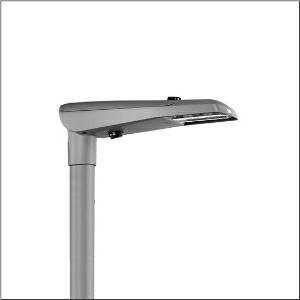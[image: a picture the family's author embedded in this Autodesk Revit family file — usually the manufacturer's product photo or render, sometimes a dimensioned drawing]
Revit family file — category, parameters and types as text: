
# Revit family: streetlight_sl_11_iq_micro___st1_2a_5xc1ac1y08de_0507
name_source: partatom
category: Lighting Fixtures
units: mm (PartAtom-declared; Revit-internal decimal feet)

## family parameters
Cut with Voids When Loaded = No
Host = Face
Light Source = No
Part Type = Normal
Room Calculation Point = No
Round Connector Dimension = Use Diameter
Shared = No

## types (1)
- --- (1 x LED, 3860 lm, 27.3 W, 4000K)
    Apparent Load = 27 VA
    CIE Flux Codes = 33 71 96 100 100
    Color Rendering = 70
    Color Temperature = 4000K
    Default Elevation = 1800 mm
    Description = Streetlight SL 11 iQ micro, mast luminaire, primary light control with 3 zone facetted reflector, of plastic, silver coated, highly specular, primary optical cover: cover, of PMMA, transparent, light distribution: ST1.2a, light emission: direct distribution, primary light characteristic: asymmetric, installation type: post-top, side-entry, lamps: LED, High Power LED, rated values: 3.620lm | 27,1W | 133,6lm/W (begin service life); end service life: 3.620lm | 27,6W; at 50% lumin. flux: 1.810lm | 13,3W | 136,1lm/W, colour temperature: 2200/2700/3000/4000K, colour rendering: CRI > 70, light colour: 722/727/730/740, light setting 1 begin service life: 100% | 3.620lm | 27,1W | 133,6lm/W | 3.000K, light setting 1 end service life: 27,6W, further light settings possible, control: pre-setting: logarithmic dimming characteristic, Street-Remote, Auto-Match, Temp-Guard, Lumen-Switch, Night-Set, Smart-Wire, Light-Fading, Desk-Remote (wireless, voltage-free reading and setting of iQ features in the workshop via application-optimized NFC function/RFID function), optimised constant luminous flux control (CLO 2.0), with cable H07RN-F 5x 1.5mm², mains connection: 220..240V, AC, 50/60Hz, connection cable pre-assembled, cable length: 6,5m, luminaire housing, of diecast aluminium, powder-coated, Siteco® metallic grey (DB 702S), please order mast flange separately, inclination adjustable without tools: 0°, 5°, 10°, 15° (post-top) | 0°, -5°, -10°, -15° (side-entry), sealing non-destructively replaceable, multi-level sealing system, length: 600mm, width: 174mm, height: 116mm, mast flange for spigot size: 42mm (side-entry): 5XC10008XM4, 60/48mm (side-entry/post-top): 5XC10108XM2, 76/60mm (side-entry/post-top): 5XC10108XM1, equipment: Power, Smart Interface below and above, protection rating (complete): IP66, insulation class (complete): insulation class II (safety insulation), certification: CE, ENEC, ENEC+, VDE, UKCA, impact resistance: IK10, permissible operating ambient temperature for outdoor applications: -25..+50°C, standard-compliant lighting for roads and squares, Environmental Product Declaration (EPD) tested and certified by an independent institute, packaging unit: 1 piece

Light Distribution: ST1.2a
    Height = 116 mm
    Lamp = 1 x LED
    Lamp Light Flux = 3860 lm
    Lamp Power = 27.3 W
    Lamp count = 1
    Length = 600 mm
    Luminous efficacy = 141 lm/W
    Manufacturer = Siteco
    ModVariant = No
    Model = 5XC1AC1Y08DE
    Number of Poles = 1
    OnlyDefault = Yes
    Power Factor = 1
    Product Name = Streetlight SL 11 iQ micro | ST1.2a
    Product group = mast luminaire | pylon top
    ProductGroupID = 6100
    Protection Class = Protection class II
    Protection Degree = IP 66
    RLX_Detail_Level = 1
    RLX_Emergency_Light_Flux = 0 lm
    RLX_Emergency_Type = 0
    RLX_Emergency_Type_DB = No
    RlxData = <blob elided: 59425 chars, md5=b5e625f8>
    Socket = socket
    Standby Power = 0 W
    System Light Flux = 3860 lm
    System Power = 27 W
    Type Comments = individual setting: luminous flux: 100 % | dim-lin: 254 | 726 mA
    Type Image = l_1005956.jpg
    URL = http://relux.com
    VarID = @adj_065615
    Voltage = 0 V
    Weight = 0.00 kg
    Width = 174 mm

## geometry (parser evidence)
native form markers: Blend x4, Sweep x11
no freeform markers — native parametric forms only
